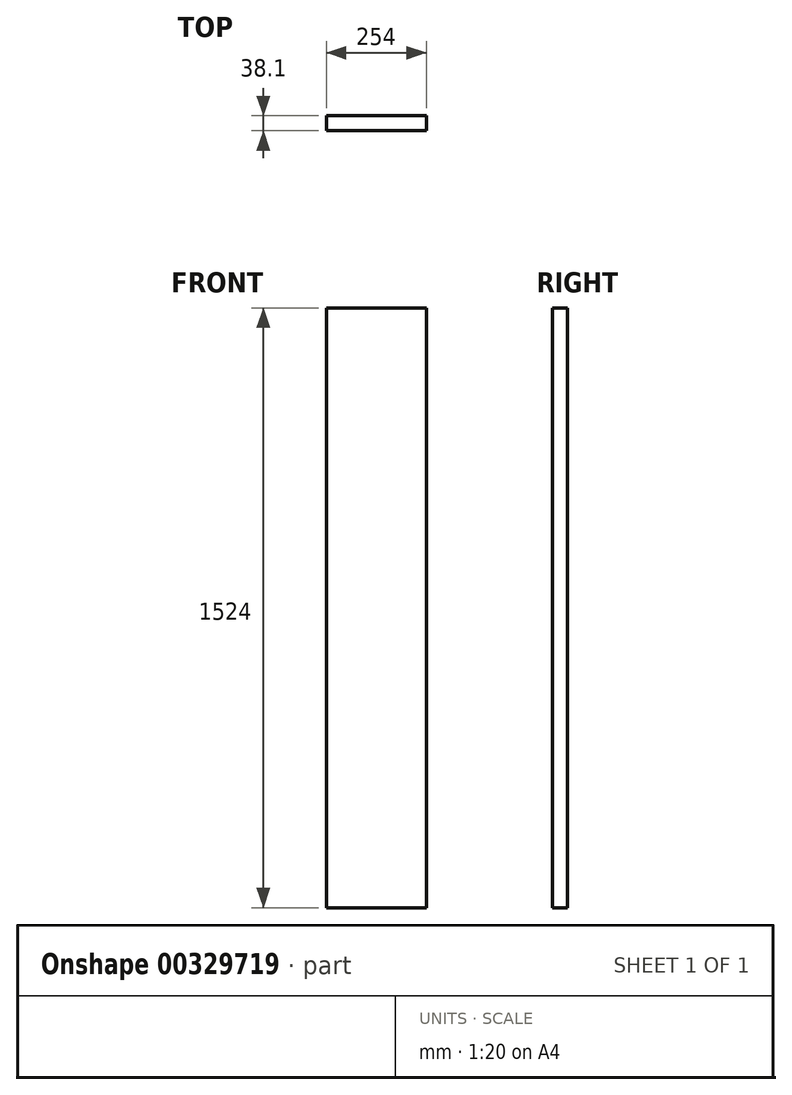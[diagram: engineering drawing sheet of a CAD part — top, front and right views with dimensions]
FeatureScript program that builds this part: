
annotation { "Feature Type Name" : "Feature", "Feature Type Description" : "" }
export const myFeature = defineFeature(function(context is Context, id is Id, definition is map)
    precondition{}
    {
        {
            var Q0;
            Q0=qCreatedBy(makeId("Front.planeOp"),FACE);
            var sketch = newSketch(context, id + "F0", { "sketchPlane" : qUnion([Q0])});
            skLineSegment(sketch, "E0.bottom", {"start": v(-127, 762) * mm, "end": v(127, 762) * mm});
            skLineSegment(sketch, "E0.top", {"start": v(-127, -762) * mm, "end": v(127, -762) * mm});
            skLineSegment(sketch, "E0.left", {"start": v(-127, 762) * mm, "end": v(-127, -762) * mm});
            skLineSegment(sketch, "E0.right", {"start": v(127, 762) * mm, "end": v(127, -762) * mm});
            skPoint(sketch, "E0.middle", {"position": v(0, 0) * mm});
            skSolve(sketch);
        }
        {
            var Q0;
            Q0=makeQuery(id+"F0.imprint","IMPRINT",FACE,{"disambiguationData":[TD([[makeQuery(id+"F0.imprint","IMPRINT",EDGE,{"derivedFrom":sQuery(id+"F0.wireOp",EDGE,"E0.bottom")}),-1.0]])]});
            extrude(context, id + "F1", {"entities" : qUnion([Q0]), "endBound" : BoundingType.SYMMETRIC, "depth" : 38.1 * mm});
        }
    });
